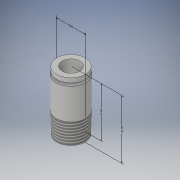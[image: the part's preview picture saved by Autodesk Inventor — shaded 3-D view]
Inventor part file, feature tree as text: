
AUTODESK INVENTOR PART (.ipt)
format: ipt  version: 2024.3 (Build 283343000, 343)  size: 171,008 bytes
history: native  units: mm
features: other x11, sketch x3, revolve x2, extrude x2, thread x1
ambient origin geometry x8: Origin, YZ Plane, XZ Plane, XY Plane, X Axis, Y Axis, Z Axis, Center Point
bodies: Solid1 (feature_tree)
feature tree (19):
  other  "Annotations"
  revolve  "Revolution1"  [1 undecoded]
  thread  "Thread1"  [1 undecoded]
  extrude  "Extrusion1"  Depth=18.8mm TaperAngle=0.0deg
  revolve  "Revolution2"  [1 undecoded]
  extrude  "Extrusion2"  [1 undecoded]
  other  "CNS_SCREW_XY"
  other  "CNS_SCREW_YZ"
  other  "CNS_SCREW_ZX"
  other  "CNS_SCREW_X"
  other  "CNS_SCREW_Y"
  other  "CNS_SCREW_Z"
  other  "CNS_SCREW_Center"
  sketch  "Sketch_1"  dims[d0=360.0deg d1=7.97388mm d2=0.0mm d3=19.456mm d4=0.0mm]
  sketch  "Sketch_2"  dims[d5=360.0deg d6=18.8mm d7=0.0mm]
  sketch  "Sketch_3"  dims[d10=10.0mm d8=16.9mm d9=20.0mm]
  other  "Linear Dimension 1"
  other  "Linear Dimension 2"
  other  "Linear Dimension 3"
note: 4 required parameter values undecoded (feature->parameter linkage not recoverable at this tier; creation-order binding heuristic only, values carry confidence <= 0.55)